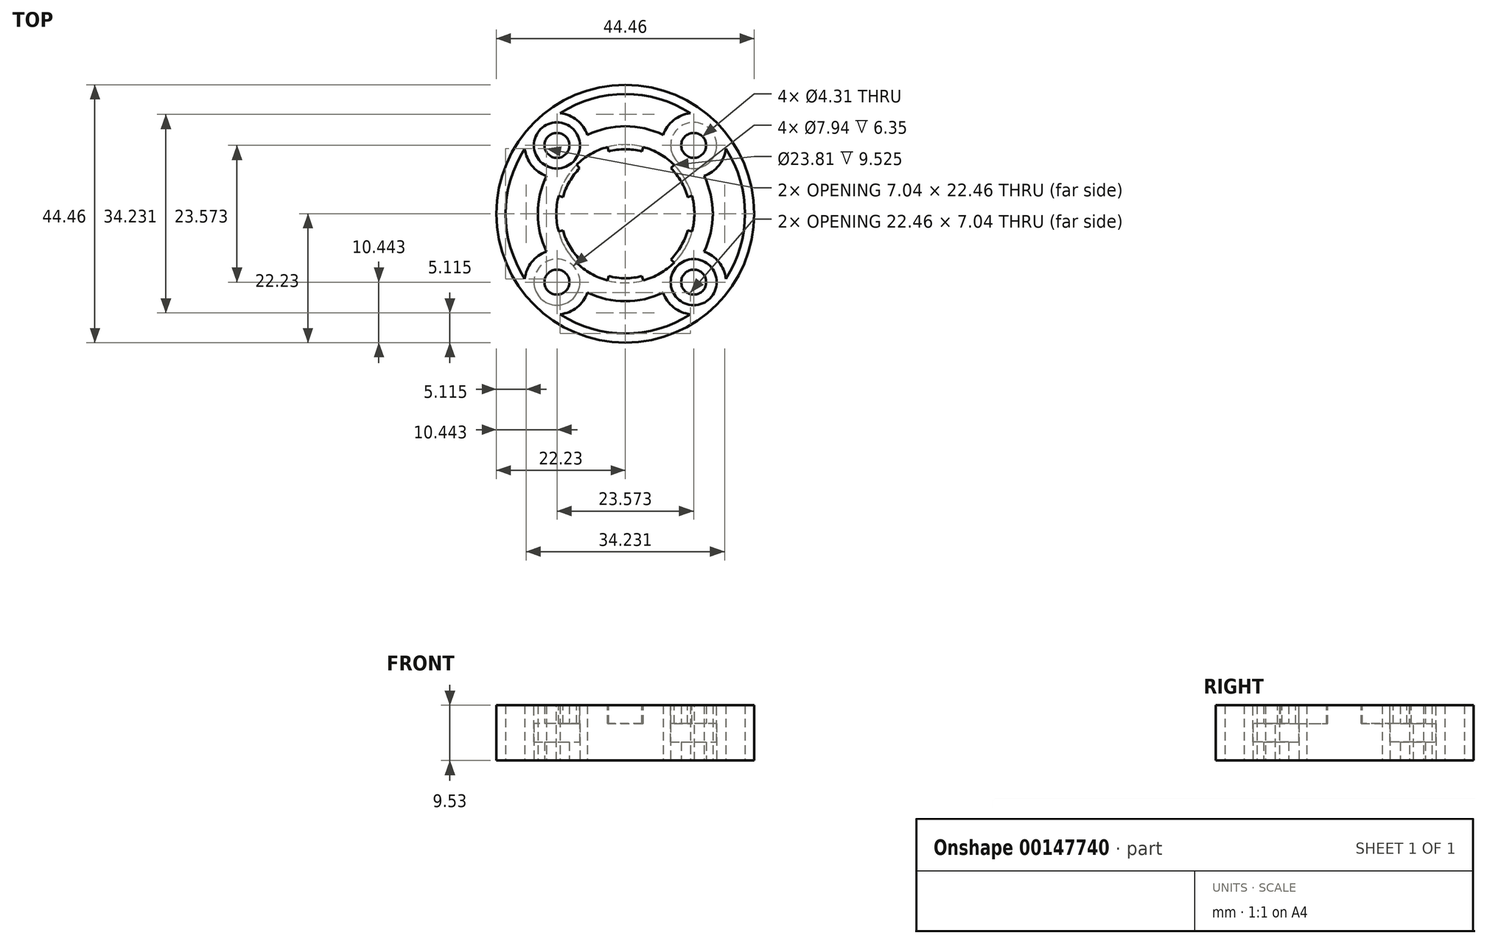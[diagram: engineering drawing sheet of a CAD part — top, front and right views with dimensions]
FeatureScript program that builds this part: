
annotation { "Feature Type Name" : "Feature", "Feature Type Description" : "" }
export const myFeature = defineFeature(function(context is Context, id is Id, definition is map)
    precondition{}
    {
        {
            var Q0;
            Q0=qCreatedBy(makeId("Top.planeOp"),FACE);
            var sketch = newSketch(context, id + "F0", { "sketchPlane" : qUnion([Q0])});
            skCircle(sketch, "E0", {"center": v(0, 0) * mm, "radius": 11.11 * mm});
            skLineSegment(sketch, "E1.bottom", {"start": v(11.79, 11.79) * mm, "end": v(-11.79, 11.79) * mm, "construction": true});
            skLineSegment(sketch, "E1.top", {"start": v(11.79, -11.79) * mm, "end": v(-11.79, -11.79) * mm, "construction": true});
            skLineSegment(sketch, "E1.left", {"start": v(11.79, 11.79) * mm, "end": v(11.79, -11.79) * mm, "construction": true});
            skLineSegment(sketch, "E1.right", {"start": v(-11.79, 11.79) * mm, "end": v(-11.79, -11.79) * mm, "construction": true});
            skCircle(sketch, "E2", {"center": v(-11.79, 11.79) * mm, "radius": 5.56 * mm, "construction": true});
            skLineSegment(sketch, "E3", {"start": v(0, 0) * mm, "end": v(0, 11.11) * mm});
            skCircle(sketch, "E4", {"center": v(-11.79, 11.79) * mm, "radius": 2.15 * mm});
            skCircle(sketch, "E5", {"center": v(-11.79, -11.79) * mm, "radius": 2.15 * mm});
            skCircle(sketch, "E6", {"center": v(11.79, -11.79) * mm, "radius": 2.15 * mm});
            skCircle(sketch, "E7", {"center": v(11.79, 11.79) * mm, "radius": 2.15 * mm});
            skCircle(sketch, "E8", {"center": v(0, 0) * mm, "radius": 22.23 * mm});
            skSolve(sketch);
        }
        {
            var Q0;
            Q0=qSketchRegion(id+"F0",true);
            extrude(context, id + "F1", {"entities" : qUnion([Q0]), "depth" : 9.52 * mm});
        }
        {
            var Q0;
            Q0=makeQuery(id+"F1.opExtrude","CAP_FACE",FACE,{"disambiguationData":[OSD([sQuery(id+"F0.wireOp",EDGE,"E0"),sQuery(id+"F0.wireOp",EDGE,"66XUYhlC-g5MV-aD6u-Z0ay-hjDTK084ohIY.top"),sQuery(id+"F0.wireOp",EDGE,"66XUYhlC-g5MV-aD6u-Z0ay-hjDTK084ohIY.left"),sQuery(id+"F0.wireOp",EDGE,"66XUYhlC-g5MV-aD6u-Z0ay-hjDTK084ohIY.right"),sQuery(id+"F0.wireOp",EDGE,"nqN0bBuQ-hJ1m-BtXy-d5jW-CiUxEReohyUV"),sQuery(id+"F0.wireOp",EDGE,"E4"),sQuery(id+"F0.wireOp",EDGE,"E5"),sQuery(id+"F0.wireOp",EDGE,"E6"),sQuery(id+"F0.wireOp",EDGE,"E7")])],"isStart":false});
            var sketch = newSketch(context, id + "F2", { "sketchPlane" : qUnion([Q0])});
            skLineSegment(sketch, "E9", {"start": v(0, 0) * mm, "end": v(-5.56, 9.62) * mm, "construction": true});
            skLineSegment(sketch, "E10", {"start": v(0, 0) * mm, "end": v(-2.88, 10.73) * mm, "construction": true});
            skLineSegment(sketch, "E11", {"start": v(0, 0) * mm, "end": v(-7.86, 7.86) * mm, "construction": true});
            skArc(sketch, "E12", {"start": v(-2.88, 10.73) * mm, "mid": v(-5.56, 9.62) * mm, "end": v(-7.86, 7.86) * mm});
            skLineSegment(sketch, "E13", {"start": v(-7.86, 7.86) * mm, "end": v(-8.42, 8.42) * mm});
            skLineSegment(sketch, "E14", {"start": v(-2.88, 10.73) * mm, "end": v(-3.08, 11.5) * mm});
            skArc(sketch, "E15", {"start": v(-3.08, 11.5) * mm, "mid": v(-5.95, 10.31) * mm, "end": v(-8.42, 8.42) * mm});
            skLineSegment(sketch, "E16", {"start": v(0, 0) * mm, "end": v(0, 11.11) * mm, "construction": true});
            skSolve(sketch);
        }
        {
            var Q0;
            Q0=qSketchRegion(id+"F2",true);
            var Q1;
            Q1=makeQuery(id+"F1.opExtrude","CAP_FACE",FACE,{"disambiguationData":[OSD([sQuery(id+"F0.wireOp",EDGE,"E0"),sQuery(id+"F0.wireOp",EDGE,"66XUYhlC-g5MV-aD6u-Z0ay-hjDTK084ohIY.top"),sQuery(id+"F0.wireOp",EDGE,"66XUYhlC-g5MV-aD6u-Z0ay-hjDTK084ohIY.left"),sQuery(id+"F0.wireOp",EDGE,"66XUYhlC-g5MV-aD6u-Z0ay-hjDTK084ohIY.right"),sQuery(id+"F0.wireOp",EDGE,"nqN0bBuQ-hJ1m-BtXy-d5jW-CiUxEReohyUV"),sQuery(id+"F0.wireOp",EDGE,"E4"),sQuery(id+"F0.wireOp",EDGE,"E5"),sQuery(id+"F0.wireOp",EDGE,"E6"),sQuery(id+"F0.wireOp",EDGE,"E7")])],"isStart":true});
            extrude(context, id + "F3", {"entities" : qUnion([Q0]), "operationType" : NewBodyOperationType.REMOVE, "endBound" : BoundingType.UP_TO_SURFACE, "oppositeDirection" : true, "endBoundEntityFace" : qUnion([Q1]), "depth" : 25.4 * mm});
        }
        {
            var Q0;
            Q0=makeQuery(id+"F3.boolean.opBoolean","COPY",FACE,{"derivedFrom":makeQuery(id+"F3.opExtrude","SWEPT_FACE",FACE,{"disambiguationData":[OSD([sQuery(id+"F2.wireOp",EDGE,"E15")])]})});
            var Q1;
            Q1=makeQuery(id+"F3.boolean.opBoolean","COPY",FACE,{"derivedFrom":makeQuery(id+"F3.opExtrude","SWEPT_FACE",FACE,{"disambiguationData":[OSD([sQuery(id+"F2.wireOp",EDGE,"E13")])]})});
            var Q2;
            Q2=makeQuery(id+"F3.boolean.opBoolean","COPY",FACE,{"derivedFrom":makeQuery(id+"F3.opExtrude","SWEPT_FACE",FACE,{"disambiguationData":[OSD([sQuery(id+"F2.wireOp",EDGE,"E14")])]})});
            var Q3;
            Q3=makeQuery(id+"F1.opExtrude","SWEPT_FACE",FACE,{"disambiguationData":[OSD([sQuery(id+"F0.wireOp",EDGE,"E0")])]});
            circularPattern(context, id + "F4", {"patternType" : PatternType.FACE, "faces" : qUnion([Q0, Q1, Q2]), "axis" : qUnion([Q3]), "angle" : 60 * degree, "instanceCount" : 6});
        }
        {
            var Q0;
            Q0=makeQuery(id+"F1.opExtrude","CAP_FACE",FACE,{"disambiguationData":[OSD([sQuery(id+"F0.wireOp",EDGE,"E0"),sQuery(id+"F0.wireOp",EDGE,"E4"),sQuery(id+"F0.wireOp",EDGE,"E5"),sQuery(id+"F0.wireOp",EDGE,"E6"),sQuery(id+"F0.wireOp",EDGE,"E7"),sQuery(id+"F0.wireOp",EDGE,"E8")])],"isStart":false});
            cPlane(context, id + "F5", {"entities" : qUnion([Q0]), "cplaneType" : CPlaneType.OFFSET, "offset" : 3.17 * mm, "oppositeDirection" : true, "width" : 152.4 * mm, "height" : 152.4 * mm});
        }
        {
            var Q0;
            Q0=makeQuery(id+"F1.opExtrude","CAP_FACE",FACE,{"disambiguationData":[OSD([sQuery(id+"F0.wireOp",EDGE,"E0"),sQuery(id+"F0.wireOp",EDGE,"E4"),sQuery(id+"F0.wireOp",EDGE,"E5"),sQuery(id+"F0.wireOp",EDGE,"E6"),sQuery(id+"F0.wireOp",EDGE,"E7"),sQuery(id+"F0.wireOp",EDGE,"E8")])],"isStart":true});
            var sketch = newSketch(context, id + "F6", { "sketchPlane" : qUnion([Q0])});
            skCircle(sketch, "E17", {"center": v(0, 0) * mm, "radius": 11.9 * mm});
            skSolve(sketch);
        }
        {
            var Q0;
            Q0=qSketchRegion(id+"F6",true);
            var Q1;
            Q1=qCreatedBy(id+"F5.planeOp",FACE);
            extrude(context, id + "F7", {"entities" : qUnion([Q0]), "operationType" : NewBodyOperationType.REMOVE, "endBound" : BoundingType.UP_TO_SURFACE, "oppositeDirection" : true, "endBoundEntityFace" : qUnion([Q1]), "depth" : 25.4 * mm});
        }
        {
            var Q0;
            Q0=makeQuery(id+"F1.opExtrude","CAP_FACE",FACE,{"disambiguationData":[OSD([sQuery(id+"F0.wireOp",EDGE,"E0"),sQuery(id+"F0.wireOp",EDGE,"E4"),sQuery(id+"F0.wireOp",EDGE,"E5"),sQuery(id+"F0.wireOp",EDGE,"E6"),sQuery(id+"F0.wireOp",EDGE,"E7"),sQuery(id+"F0.wireOp",EDGE,"E8")])],"isStart":true});
            cPlane(context, id + "F8", {"entities" : qUnion([Q0]), "cplaneType" : CPlaneType.OFFSET, "offset" : 3.17 * mm, "oppositeDirection" : true, "width" : 152.4 * mm, "height" : 152.4 * mm});
        }
        {
            var Q0;
            Q0=makeQuery(id+"F1.opExtrude","CAP_FACE",FACE,{"disambiguationData":[OSD([sQuery(id+"F0.wireOp",EDGE,"E0"),sQuery(id+"F0.wireOp",EDGE,"E4"),sQuery(id+"F0.wireOp",EDGE,"E5"),sQuery(id+"F0.wireOp",EDGE,"E6"),sQuery(id+"F0.wireOp",EDGE,"E7"),sQuery(id+"F0.wireOp",EDGE,"E8")])],"isStart":false});
            cPlane(context, id + "F9", {"entities" : qUnion([Q0]), "cplaneType" : CPlaneType.OFFSET, "offset" : 3.17 * mm, "oppositeDirection" : true, "width" : 152.4 * mm, "height" : 152.4 * mm});
        }
        {
            var Q0;
            Q0=makeQuery(id+"F1.opExtrude","CAP_FACE",FACE,{"disambiguationData":[OSD([sQuery(id+"F0.wireOp",EDGE,"E0"),sQuery(id+"F0.wireOp",EDGE,"E4"),sQuery(id+"F0.wireOp",EDGE,"E5"),sQuery(id+"F0.wireOp",EDGE,"E6"),sQuery(id+"F0.wireOp",EDGE,"E7"),sQuery(id+"F0.wireOp",EDGE,"E8")])],"isStart":true});
            var sketch = newSketch(context, id + "F10", { "sketchPlane" : qUnion([Q0])});
            skCircle(sketch, "E18", {"center": v(11.79, -11.79) * mm, "radius": 3.97 * mm});
            skCircle(sketch, "E19", {"center": v(-11.79, 11.79) * mm, "radius": 3.97 * mm});
            skSolve(sketch);
        }
        {
            var Q0;
            Q0=qSketchRegion(id+"F10",true);
            var Q1;
            Q1=qCreatedBy(id+"F9.planeOp",FACE);
            extrude(context, id + "F11", {"entities" : qUnion([Q0]), "operationType" : NewBodyOperationType.REMOVE, "endBound" : BoundingType.UP_TO_SURFACE, "oppositeDirection" : true, "endBoundEntityFace" : qUnion([Q1]), "depth" : 25.4 * mm});
        }
        {
            var Q0;
            Q0=makeQuery(id+"F1.opExtrude","CAP_FACE",FACE,{"disambiguationData":[OSD([sQuery(id+"F0.wireOp",EDGE,"E0"),sQuery(id+"F0.wireOp",EDGE,"E4"),sQuery(id+"F0.wireOp",EDGE,"E5"),sQuery(id+"F0.wireOp",EDGE,"E6"),sQuery(id+"F0.wireOp",EDGE,"E7"),sQuery(id+"F0.wireOp",EDGE,"E8")])],"isStart":false});
            var sketch = newSketch(context, id + "F12", { "sketchPlane" : qUnion([Q0])});
            skCircle(sketch, "E20", {"center": v(-11.79, 11.79) * mm, "radius": 3.97 * mm});
            skCircle(sketch, "E21", {"center": v(11.79, -11.79) * mm, "radius": 3.97 * mm});
            skSolve(sketch);
        }
        {
            var Q0;
            Q0=qSketchRegion(id+"F12",true);
            var Q1;
            Q1=qCreatedBy(id+"F8.planeOp",FACE);
            extrude(context, id + "F13", {"entities" : qUnion([Q0]), "operationType" : NewBodyOperationType.REMOVE, "endBound" : BoundingType.UP_TO_SURFACE, "oppositeDirection" : true, "endBoundEntityFace" : qUnion([Q1]), "depth" : 25.4 * mm});
        }
        {
            var Q0;
            Q0=makeQuery(id+"F1.opExtrude","CAP_FACE",FACE,{"disambiguationData":[OSD([sQuery(id+"F0.wireOp",EDGE,"E0"),sQuery(id+"F0.wireOp",EDGE,"E4"),sQuery(id+"F0.wireOp",EDGE,"E5"),sQuery(id+"F0.wireOp",EDGE,"E6"),sQuery(id+"F0.wireOp",EDGE,"E7"),sQuery(id+"F0.wireOp",EDGE,"E8")])],"isStart":true});
            var sketch = newSketch(context, id + "F14", { "sketchPlane" : qUnion([Q0])});
            skArc(sketch, "E22", {"start": v(6.53, -13.6) * mm, "mid": v(8.34, -16.14) * mm, "end": v(11.23, -17.31) * mm});
            skArc(sketch, "E23", {"start": v(-11.23, -17.31) * mm, "mid": v(0, -20.64) * mm, "end": v(11.23, -17.31) * mm});
            skArc(sketch, "E24", {"start": v(-6.53, -13.6) * mm, "mid": v(0, -15.08) * mm, "end": v(6.53, -13.6) * mm});
            skArc(sketch, "E25", {"start": v(-11.23, -17.31) * mm, "mid": v(-8.34, -16.14) * mm, "end": v(-6.53, -13.6) * mm});
            skLineSegment(sketch, "E26", {"start": v(11.23, -17.31) * mm, "end": v(0, 0) * mm, "construction": true});
            skLineSegment(sketch, "E27", {"start": v(0, 0) * mm, "end": v(-11.23, -17.31) * mm, "construction": true});
            skSolve(sketch);
        }
        {
            var Q0;
            Q0=qSketchRegion(id+"F14",true);
            var Q1;
            Q1=makeQuery(id+"F1.opExtrude","CAP_FACE",FACE,{"disambiguationData":[OSD([sQuery(id+"F0.wireOp",EDGE,"E0"),sQuery(id+"F0.wireOp",EDGE,"E4"),sQuery(id+"F0.wireOp",EDGE,"E5"),sQuery(id+"F0.wireOp",EDGE,"E6"),sQuery(id+"F0.wireOp",EDGE,"E7"),sQuery(id+"F0.wireOp",EDGE,"E8")])],"isStart":false});
            extrude(context, id + "F15", {"entities" : qUnion([Q0]), "operationType" : NewBodyOperationType.REMOVE, "endBound" : BoundingType.UP_TO_SURFACE, "oppositeDirection" : true, "endBoundEntityFace" : qUnion([Q1]), "depth" : 25.4 * mm});
        }
        {
            var Q0;
            Q0=makeQuery(id+"F15.boolean.opBoolean","COPY",FACE,{"derivedFrom":makeQuery(id+"F15.opExtrude","SWEPT_FACE",FACE,{"disambiguationData":[OSD([sQuery(id+"F14.wireOp",EDGE,"E23")])]})});
            var Q1;
            Q1=makeQuery(id+"F15.boolean.opBoolean","COPY",FACE,{"derivedFrom":makeQuery(id+"F15.opExtrude","SWEPT_FACE",FACE,{"disambiguationData":[OSD([sQuery(id+"F14.wireOp",EDGE,"E25")])]})});
            var Q2;
            Q2=makeQuery(id+"F15.boolean.opBoolean","COPY",FACE,{"derivedFrom":makeQuery(id+"F15.opExtrude","SWEPT_FACE",FACE,{"disambiguationData":[OSD([sQuery(id+"F14.wireOp",EDGE,"E24")])]})});
            var Q3;
            Q3=makeQuery(id+"F15.boolean.opBoolean","COPY",FACE,{"derivedFrom":makeQuery(id+"F15.opExtrude","SWEPT_FACE",FACE,{"disambiguationData":[OSD([sQuery(id+"F14.wireOp",EDGE,"E22")])]})});
            var Q4;
            Q4=makeQuery(id+"F1.opExtrude","SWEPT_FACE",FACE,{"disambiguationData":[OSD([sQuery(id+"F0.wireOp",EDGE,"E8")])]});
            circularPattern(context, id + "F16", {"patternType" : PatternType.FACE, "faces" : qUnion([Q0, Q1, Q2, Q3]), "axis" : qUnion([Q4]), "angle" : 90 * degree, "instanceCount" : 4});
        }
    });
